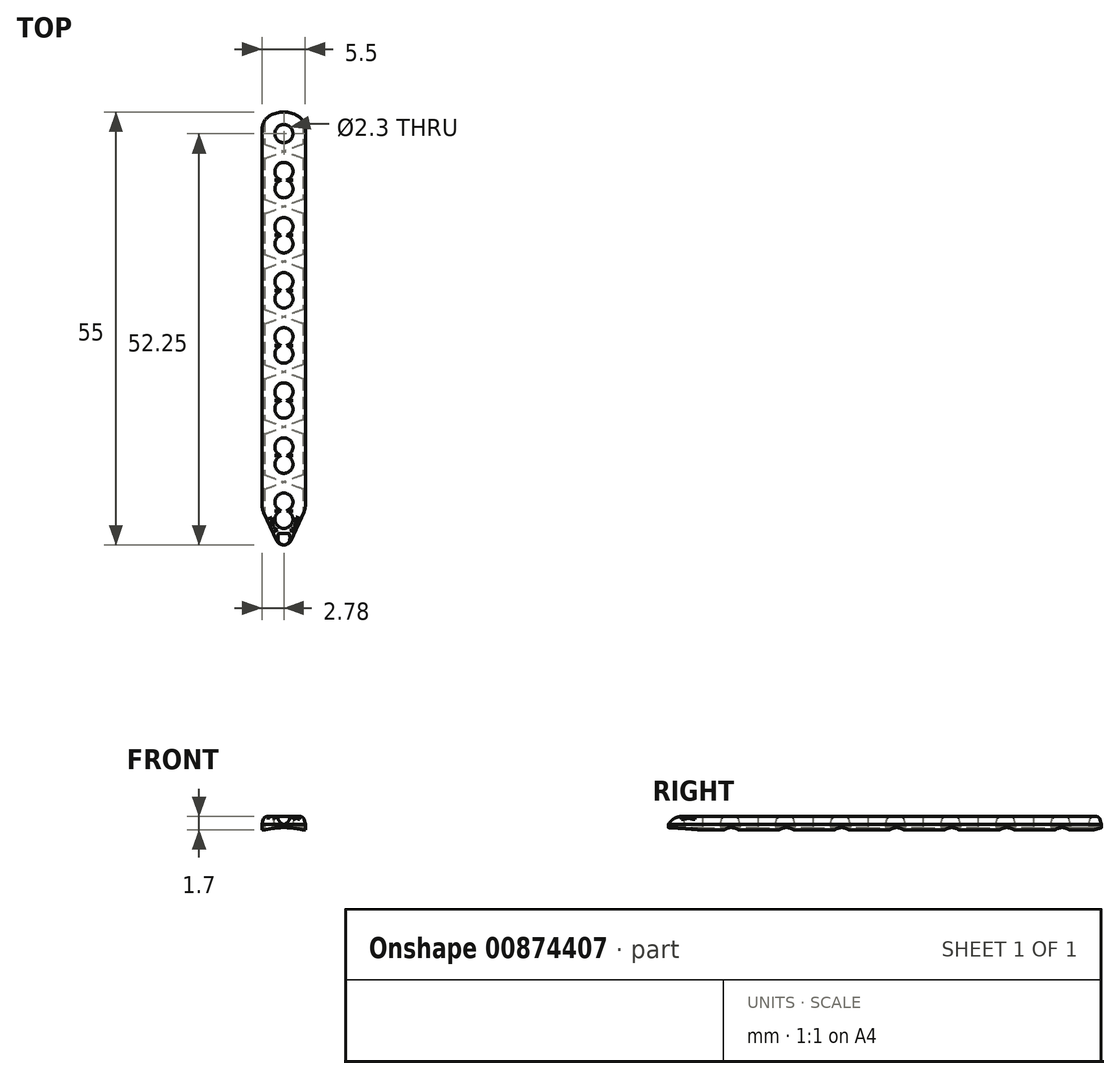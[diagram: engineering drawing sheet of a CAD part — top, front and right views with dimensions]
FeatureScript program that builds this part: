
annotation { "Feature Type Name" : "Feature", "Feature Type Description" : "" }
export const myFeature = defineFeature(function(context is Context, id is Id, definition is map)
    precondition{}
    {
        {
            var Q0;
            Q0=qCreatedBy(makeId("Top.planeOp"),FACE);
            var sketch = newSketch(context, id + "F0", { "sketchPlane" : qUnion([Q0])});
            skLineSegment(sketch, "E0", {"start": v(0, 0) * mm, "end": v(0, -52.25) * mm, "construction": true});
            skLineSegment(sketch, "E1", {"start": v(-2.78, -47.25) * mm, "end": v(-2.78, 0.55) * mm});
            skLineSegment(sketch, "E2", {"start": v(-2.78, 1.42) * mm, "end": v(2.72, 1.42) * mm, "construction": true});
            skLineSegment(sketch, "E3", {"start": v(2.72, 0.57) * mm, "end": v(2.72, -47.25) * mm});
            skArc(sketch, "E4", {"start": v(1.77, 2.26) * mm, "mid": v(0, 2.75) * mm, "end": v(-1.78, 2.28) * mm});
            skLineSegment(sketch, "E5", {"start": v(0, 2.75) * mm, "end": v(0, 0) * mm});
            skPoint(sketch, "E6.visualSharp", {"position": v(-2.78, 1.42) * mm});
            skArc(sketch, "E6.filletArc", {"start": v(-1.78, 2.28) * mm, "mid": v(-2.5, 1.55) * mm, "end": v(-2.78, 0.55) * mm});
            skPoint(sketch, "E7.visualSharp", {"position": v(2.72, 1.42) * mm});
            skArc(sketch, "E7.filletArc", {"start": v(2.72, 0.57) * mm, "mid": v(2.47, 1.54) * mm, "end": v(1.77, 2.26) * mm});
            skPoint(sketch, "E8.visualSharp", {"position": v(0, -52.25) * mm});
            skArc(sketch, "E8.filletArc", {"start": v(-0.91, -51.67) * mm, "mid": v(0, -52.25) * mm, "end": v(0.9, -51.67) * mm});
            skCircle(sketch, "E9", {"center": v(0, 0) * mm, "radius": 1.15 * mm, "construction": true});
            skPoint(sketch, "E10", {"position": v(0, 1.15) * mm});
            skLineSegment(sketch, "E11", {"start": v(-2.78, -47.25) * mm, "end": v(2.72, -47.25) * mm, "construction": true});
            skLineSegment(sketch, "E12", {"start": v(-2.59, -48.1) * mm, "end": v(-0.91, -51.67) * mm});
            skLineSegment(sketch, "E13", {"start": v(0.9, -51.67) * mm, "end": v(2.54, -48.08) * mm});
            skArc(sketch, "E14", {"start": v(-2.78, -47.25) * mm, "mid": v(-2.73, -47.68) * mm, "end": v(-2.59, -48.1) * mm});
            skArc(sketch, "E15", {"start": v(2.54, -48.08) * mm, "mid": v(2.68, -47.68) * mm, "end": v(2.72, -47.25) * mm});
            skSolve(sketch);
        }
        {
            var Q0;
            Q0=makeQuery(id+"F0.imprint","IMPRINT",FACE,{"disambiguationData":[TD([[makeQuery(id+"F0.imprint","IMPRINT",EDGE,{"derivedFrom":sQuery(id+"F0.wireOp",EDGE,"E1")}),-1.0]])]});
            extrude(context, id + "F1", {"entities" : qUnion([Q0]), "depth" : 1.7 * mm, "offsetDistance" : 25 * mm});
        }
        {
            var Q0;
            Q0=qCreatedBy(makeId("Right.planeOp"),FACE);
            var sketch = newSketch(context, id + "F2", { "sketchPlane" : qUnion([Q0])});
            skCircle(sketch, "E16", {"center": v(-44.25, -1.2) * mm, "radius": 1.5 * mm});
            skPoint(sketch, "E17", {"position": v(-44.25, 0.3) * mm});
            skPoint(sketch, "E18", {"position": v(-44.25, 0) * mm});
            skCircle(sketch, "E19.1.0.0", {"center": v(-37.25, -1.2) * mm, "radius": 1.5 * mm});
            skCircle(sketch, "E19.2.0.0", {"center": v(-30.25, -1.2) * mm, "radius": 1.5 * mm});
            skCircle(sketch, "E19.3.0.0", {"center": v(-23.25, -1.2) * mm, "radius": 1.5 * mm});
            skCircle(sketch, "E19.4.0.0", {"center": v(-16.25, -1.2) * mm, "radius": 1.5 * mm});
            skCircle(sketch, "E19.5.0.0", {"center": v(-9.25, -1.2) * mm, "radius": 1.5 * mm});
            skCircle(sketch, "E19.6.0.0", {"center": v(-2.25, -1.2) * mm, "radius": 1.5 * mm});
            skLineSegment(sketch, "E19.direction1", {"start": v(-44.25, -1.2) * mm, "end": v(-37.25, -1.2) * mm, "construction": true});
            skSolve(sketch);
        }
        {
            var Q0;
            Q0 = qSketchRegion(id + "F2", true);
            extrude(context, id + "F3", {"entities" : qUnion([Q0]), "operationType" : NewBodyOperationType.REMOVE, "depth" : 25 * mm, "offsetDistance" : 25 * mm, "hasSecondDirection" : true, "secondDirectionOppositeDirection" : true, "secondDirectionDepth" : 25 * mm});
        }
        {
            var Q0;
            Q0=qCreatedBy(makeId("Top.planeOp"),FACE);
            var sketch = newSketch(context, id + "F4", { "sketchPlane" : qUnion([Q0])});
            skCircle(sketch, "E20", {"center": v(0, 0) * mm, "radius": 1.15 * mm});
            skArc(sketch, "E21", {"start": v(0.34, -5.9) * mm, "mid": v(0, -3.65) * mm, "end": v(-0.34, -5.9) * mm});
            skArc(sketch, "E22", {"start": v(-0.34, -5.9) * mm, "mid": v(0, -8.15) * mm, "end": v(0.34, -5.9) * mm});
            skLineSegment(sketch, "E23", {"start": v(0, -7) * mm, "end": v(0, -4.8) * mm, "construction": true});
            skPoint(sketch, "E24", {"position": v(0, -3.65) * mm});
            skPoint(sketch, "E25", {"position": v(0, -8.15) * mm});
            skPoint(sketch, "E26", {"position": v(0, -1.15) * mm});
            skArc(sketch, "E27.0.1.0", {"start": v(0.34, -12.9) * mm, "mid": v(0, -10.65) * mm, "end": v(-0.34, -12.9) * mm});
            skArc(sketch, "E27.0.1.1", {"start": v(-0.34, -12.9) * mm, "mid": v(0, -15.15) * mm, "end": v(0.34, -12.9) * mm});
            skLineSegment(sketch, "E27.0.1.2", {"start": v(0, -14) * mm, "end": v(0, -11.8) * mm, "construction": true});
            skArc(sketch, "E27.0.2.0", {"start": v(0.34, -19.9) * mm, "mid": v(0, -17.65) * mm, "end": v(-0.34, -19.9) * mm});
            skArc(sketch, "E27.0.2.1", {"start": v(-0.34, -19.9) * mm, "mid": v(0, -22.15) * mm, "end": v(0.34, -19.9) * mm});
            skLineSegment(sketch, "E27.0.2.2", {"start": v(0, -21) * mm, "end": v(0, -18.8) * mm, "construction": true});
            skArc(sketch, "E27.0.3.0", {"start": v(0.34, -26.9) * mm, "mid": v(0, -24.65) * mm, "end": v(-0.34, -26.9) * mm});
            skArc(sketch, "E27.0.3.1", {"start": v(-0.34, -26.9) * mm, "mid": v(0, -29.15) * mm, "end": v(0.34, -26.9) * mm});
            skLineSegment(sketch, "E27.0.3.2", {"start": v(0, -28) * mm, "end": v(0, -25.8) * mm, "construction": true});
            skArc(sketch, "E27.0.4.0", {"start": v(0.34, -33.9) * mm, "mid": v(0, -31.65) * mm, "end": v(-0.34, -33.9) * mm});
            skArc(sketch, "E27.0.4.1", {"start": v(-0.34, -33.9) * mm, "mid": v(0, -36.15) * mm, "end": v(0.34, -33.9) * mm});
            skLineSegment(sketch, "E27.0.4.2", {"start": v(0, -35) * mm, "end": v(0, -32.8) * mm, "construction": true});
            skArc(sketch, "E27.0.5.0", {"start": v(0.34, -40.9) * mm, "mid": v(0, -38.65) * mm, "end": v(-0.34, -40.9) * mm});
            skArc(sketch, "E27.0.5.1", {"start": v(-0.34, -40.9) * mm, "mid": v(0, -43.15) * mm, "end": v(0.34, -40.9) * mm});
            skLineSegment(sketch, "E27.0.5.2", {"start": v(0, -42) * mm, "end": v(0, -39.8) * mm, "construction": true});
            skArc(sketch, "E27.0.6.0", {"start": v(0.34, -47.9) * mm, "mid": v(0, -45.65) * mm, "end": v(-0.34, -47.9) * mm});
            skArc(sketch, "E27.0.6.1", {"start": v(-0.34, -47.9) * mm, "mid": v(0, -50.15) * mm, "end": v(0.34, -47.9) * mm});
            skLineSegment(sketch, "E27.0.6.2", {"start": v(0, -49) * mm, "end": v(0, -46.8) * mm, "construction": true});
            skLineSegment(sketch, "E27.direction1", {"start": v(-0.34, -5.9) * mm, "end": v(11.96, -5.9) * mm, "construction": true});
            skLineSegment(sketch, "E27.direction2", {"start": v(-0.34, -5.9) * mm, "end": v(-0.34, -12.9) * mm, "construction": true});
            skSolve(sketch);
        }
        {
            var Q0;
            Q0=qCreatedBy(makeId("Right.planeOp"),FACE);
            var sketch = newSketch(context, id + "F5", { "sketchPlane" : qUnion([Q0])});
            skLineSegment(sketch, "E28", {"start": v(-52.25, 0.7) * mm, "end": v(-52.25, 1.7) * mm});
            skLineSegment(sketch, "E29", {"start": v(-52.25, 1.7) * mm, "end": v(-50.25, 1.7) * mm});
            skArc(sketch, "E30", {"start": v(-50.25, 1.7) * mm, "mid": v(-51.4, 1.5) * mm, "end": v(-52.25, 0.7) * mm});
            skSolve(sketch);
        }
        {
            var Q0;
            Q0 = qSketchRegion(id + "F4", true);
            extrude(context, id + "F6", {"entities" : qUnion([Q0]), "operationType" : NewBodyOperationType.REMOVE, "endBound" : BoundingType.THROUGH_ALL, "depth" : 25 * mm, "offsetDistance" : 25 * mm});
        }
        {
            var Q0;
            Q0=makeQuery(id+"F1.opExtrude","CAP_FACE",FACE,{"disambiguationData":[OSD([sQuery(id+"F0.wireOp",EDGE,"E1"),sQuery(id+"F0.wireOp",EDGE,"E3"),sQuery(id+"F0.wireOp",EDGE,"E4"),sQuery(id+"F0.wireOp",EDGE,"E6.filletArc"),sQuery(id+"F0.wireOp",EDGE,"E7.filletArc"),sQuery(id+"F0.wireOp",EDGE,"E8.filletArc"),sQuery(id+"F0.wireOp",EDGE,"E12"),sQuery(id+"F0.wireOp",EDGE,"E13"),sQuery(id+"F0.wireOp",EDGE,"E14"),sQuery(id+"F0.wireOp",EDGE,"E15")])],"isStart":false});
            chamfer(context, id + "F7", {"entities" : qUnion([Q0]), "chamferType" : ChamferType.TWO_OFFSETS, "width1" : 1 * mm, "oppositeDirection" : false, "width2" : 0.25 * mm, "tangentPropagation" : true});
        }
        {
            var Q0;
            {var subQ0=makeQuery(id+"F1.opExtrude","CAP_FACE",FACE,{"disambiguationData":[OSD([sQuery(id+"F0.wireOp",EDGE,"E1"),sQuery(id+"F0.wireOp",EDGE,"E3"),sQuery(id+"F0.wireOp",EDGE,"E4"),sQuery(id+"F0.wireOp",EDGE,"E6.filletArc"),sQuery(id+"F0.wireOp",EDGE,"E7.filletArc"),sQuery(id+"F0.wireOp",EDGE,"E8.filletArc"),sQuery(id+"F0.wireOp",EDGE,"E12"),sQuery(id+"F0.wireOp",EDGE,"E13"),sQuery(id+"F0.wireOp",EDGE,"E14"),sQuery(id+"F0.wireOp",EDGE,"E15")])],"isStart":false});Q0=makeQuery(id+"F7.opChamfer","BLEND_EDGE",EDGE,{"blendedFrom":[makeQuery(id+"F6.boolean.opBoolean","INTERSECT",EDGE,{"derivedFrom":[subQ0,makeQuery(id+"F6.opExtrude","SWEPT_FACE",FACE,{"disambiguationData":[OSD([sQuery(id+"F4.wireOp",EDGE,"E27.0.6.1")])]})]}),subQ0],"blendedInto":[subQ0]});}
            var Q1;
            {var subQ0=makeQuery(id+"F1.opExtrude","CAP_FACE",FACE,{"disambiguationData":[OSD([sQuery(id+"F0.wireOp",EDGE,"E1"),sQuery(id+"F0.wireOp",EDGE,"E3"),sQuery(id+"F0.wireOp",EDGE,"E4"),sQuery(id+"F0.wireOp",EDGE,"E6.filletArc"),sQuery(id+"F0.wireOp",EDGE,"E7.filletArc"),sQuery(id+"F0.wireOp",EDGE,"E8.filletArc"),sQuery(id+"F0.wireOp",EDGE,"E12"),sQuery(id+"F0.wireOp",EDGE,"E13"),sQuery(id+"F0.wireOp",EDGE,"E14"),sQuery(id+"F0.wireOp",EDGE,"E15")])],"isStart":false});Q1=makeQuery(id+"F7.opChamfer","BLEND_EDGE",EDGE,{"blendedFrom":[makeQuery(id+"F6.boolean.opBoolean","INTERSECT",EDGE,{"derivedFrom":[subQ0,makeQuery(id+"F6.opExtrude","SWEPT_FACE",FACE,{"disambiguationData":[OSD([sQuery(id+"F4.wireOp",EDGE,"E27.0.6.0")])]})]}),subQ0],"blendedInto":[subQ0]});}
            var Q2;
            {var subQ0=makeQuery(id+"F1.opExtrude","CAP_FACE",FACE,{"disambiguationData":[OSD([sQuery(id+"F0.wireOp",EDGE,"E1"),sQuery(id+"F0.wireOp",EDGE,"E3"),sQuery(id+"F0.wireOp",EDGE,"E4"),sQuery(id+"F0.wireOp",EDGE,"E6.filletArc"),sQuery(id+"F0.wireOp",EDGE,"E7.filletArc"),sQuery(id+"F0.wireOp",EDGE,"E8.filletArc"),sQuery(id+"F0.wireOp",EDGE,"E12"),sQuery(id+"F0.wireOp",EDGE,"E13"),sQuery(id+"F0.wireOp",EDGE,"E14"),sQuery(id+"F0.wireOp",EDGE,"E15")])],"isStart":false});Q2=makeQuery(id+"F7.opChamfer","BLEND_EDGE",EDGE,{"blendedFrom":[makeQuery(id+"F6.boolean.opBoolean","INTERSECT",EDGE,{"derivedFrom":[subQ0,makeQuery(id+"F6.opExtrude","SWEPT_FACE",FACE,{"disambiguationData":[OSD([sQuery(id+"F4.wireOp",EDGE,"E27.0.5.1")])]})]}),subQ0],"blendedInto":[subQ0]});}
            var Q3;
            {var subQ0=makeQuery(id+"F1.opExtrude","CAP_FACE",FACE,{"disambiguationData":[OSD([sQuery(id+"F0.wireOp",EDGE,"E1"),sQuery(id+"F0.wireOp",EDGE,"E3"),sQuery(id+"F0.wireOp",EDGE,"E4"),sQuery(id+"F0.wireOp",EDGE,"E6.filletArc"),sQuery(id+"F0.wireOp",EDGE,"E7.filletArc"),sQuery(id+"F0.wireOp",EDGE,"E8.filletArc"),sQuery(id+"F0.wireOp",EDGE,"E12"),sQuery(id+"F0.wireOp",EDGE,"E13"),sQuery(id+"F0.wireOp",EDGE,"E14"),sQuery(id+"F0.wireOp",EDGE,"E15")])],"isStart":false});Q3=makeQuery(id+"F7.opChamfer","BLEND_EDGE",EDGE,{"blendedFrom":[makeQuery(id+"F6.boolean.opBoolean","INTERSECT",EDGE,{"derivedFrom":[subQ0,makeQuery(id+"F6.opExtrude","SWEPT_FACE",FACE,{"disambiguationData":[OSD([sQuery(id+"F4.wireOp",EDGE,"E27.0.5.0")])]})]}),subQ0],"blendedInto":[subQ0]});}
            var Q4;
            {var subQ0=makeQuery(id+"F1.opExtrude","CAP_FACE",FACE,{"disambiguationData":[OSD([sQuery(id+"F0.wireOp",EDGE,"E1"),sQuery(id+"F0.wireOp",EDGE,"E3"),sQuery(id+"F0.wireOp",EDGE,"E4"),sQuery(id+"F0.wireOp",EDGE,"E6.filletArc"),sQuery(id+"F0.wireOp",EDGE,"E7.filletArc"),sQuery(id+"F0.wireOp",EDGE,"E8.filletArc"),sQuery(id+"F0.wireOp",EDGE,"E12"),sQuery(id+"F0.wireOp",EDGE,"E13"),sQuery(id+"F0.wireOp",EDGE,"E14"),sQuery(id+"F0.wireOp",EDGE,"E15")])],"isStart":false});Q4=makeQuery(id+"F7.opChamfer","BLEND_EDGE",EDGE,{"blendedFrom":[makeQuery(id+"F6.boolean.opBoolean","INTERSECT",EDGE,{"derivedFrom":[subQ0,makeQuery(id+"F6.opExtrude","SWEPT_FACE",FACE,{"disambiguationData":[OSD([sQuery(id+"F4.wireOp",EDGE,"E27.0.4.1")])]})]}),subQ0],"blendedInto":[subQ0]});}
            var Q5;
            {var subQ0=makeQuery(id+"F1.opExtrude","CAP_FACE",FACE,{"disambiguationData":[OSD([sQuery(id+"F0.wireOp",EDGE,"E1"),sQuery(id+"F0.wireOp",EDGE,"E3"),sQuery(id+"F0.wireOp",EDGE,"E4"),sQuery(id+"F0.wireOp",EDGE,"E6.filletArc"),sQuery(id+"F0.wireOp",EDGE,"E7.filletArc"),sQuery(id+"F0.wireOp",EDGE,"E8.filletArc"),sQuery(id+"F0.wireOp",EDGE,"E12"),sQuery(id+"F0.wireOp",EDGE,"E13"),sQuery(id+"F0.wireOp",EDGE,"E14"),sQuery(id+"F0.wireOp",EDGE,"E15")])],"isStart":false});Q5=makeQuery(id+"F7.opChamfer","BLEND_EDGE",EDGE,{"blendedFrom":[makeQuery(id+"F6.boolean.opBoolean","INTERSECT",EDGE,{"derivedFrom":[subQ0,makeQuery(id+"F6.opExtrude","SWEPT_FACE",FACE,{"disambiguationData":[OSD([sQuery(id+"F4.wireOp",EDGE,"E27.0.4.0")])]})]}),subQ0],"blendedInto":[subQ0]});}
            var Q6;
            {var subQ0=makeQuery(id+"F1.opExtrude","CAP_FACE",FACE,{"disambiguationData":[OSD([sQuery(id+"F0.wireOp",EDGE,"E1"),sQuery(id+"F0.wireOp",EDGE,"E3"),sQuery(id+"F0.wireOp",EDGE,"E4"),sQuery(id+"F0.wireOp",EDGE,"E6.filletArc"),sQuery(id+"F0.wireOp",EDGE,"E7.filletArc"),sQuery(id+"F0.wireOp",EDGE,"E8.filletArc"),sQuery(id+"F0.wireOp",EDGE,"E12"),sQuery(id+"F0.wireOp",EDGE,"E13"),sQuery(id+"F0.wireOp",EDGE,"E14"),sQuery(id+"F0.wireOp",EDGE,"E15")])],"isStart":false});Q6=makeQuery(id+"F7.opChamfer","BLEND_EDGE",EDGE,{"blendedFrom":[makeQuery(id+"F6.boolean.opBoolean","INTERSECT",EDGE,{"derivedFrom":[subQ0,makeQuery(id+"F6.opExtrude","SWEPT_FACE",FACE,{"disambiguationData":[OSD([sQuery(id+"F4.wireOp",EDGE,"E27.0.3.1")])]})]}),subQ0],"blendedInto":[subQ0]});}
            var Q7;
            {var subQ0=makeQuery(id+"F1.opExtrude","CAP_FACE",FACE,{"disambiguationData":[OSD([sQuery(id+"F0.wireOp",EDGE,"E1"),sQuery(id+"F0.wireOp",EDGE,"E3"),sQuery(id+"F0.wireOp",EDGE,"E4"),sQuery(id+"F0.wireOp",EDGE,"E6.filletArc"),sQuery(id+"F0.wireOp",EDGE,"E7.filletArc"),sQuery(id+"F0.wireOp",EDGE,"E8.filletArc"),sQuery(id+"F0.wireOp",EDGE,"E12"),sQuery(id+"F0.wireOp",EDGE,"E13"),sQuery(id+"F0.wireOp",EDGE,"E14"),sQuery(id+"F0.wireOp",EDGE,"E15")])],"isStart":false});Q7=makeQuery(id+"F7.opChamfer","BLEND_EDGE",EDGE,{"blendedFrom":[makeQuery(id+"F6.boolean.opBoolean","INTERSECT",EDGE,{"derivedFrom":[subQ0,makeQuery(id+"F6.opExtrude","SWEPT_FACE",FACE,{"disambiguationData":[OSD([sQuery(id+"F4.wireOp",EDGE,"E27.0.3.0")])]})]}),subQ0],"blendedInto":[subQ0]});}
            var Q8;
            {var subQ0=makeQuery(id+"F1.opExtrude","CAP_FACE",FACE,{"disambiguationData":[OSD([sQuery(id+"F0.wireOp",EDGE,"E1"),sQuery(id+"F0.wireOp",EDGE,"E3"),sQuery(id+"F0.wireOp",EDGE,"E4"),sQuery(id+"F0.wireOp",EDGE,"E6.filletArc"),sQuery(id+"F0.wireOp",EDGE,"E7.filletArc"),sQuery(id+"F0.wireOp",EDGE,"E8.filletArc"),sQuery(id+"F0.wireOp",EDGE,"E12"),sQuery(id+"F0.wireOp",EDGE,"E13"),sQuery(id+"F0.wireOp",EDGE,"E14"),sQuery(id+"F0.wireOp",EDGE,"E15")])],"isStart":false});Q8=makeQuery(id+"F7.opChamfer","BLEND_EDGE",EDGE,{"blendedFrom":[makeQuery(id+"F6.boolean.opBoolean","INTERSECT",EDGE,{"derivedFrom":[subQ0,makeQuery(id+"F6.opExtrude","SWEPT_FACE",FACE,{"disambiguationData":[OSD([sQuery(id+"F4.wireOp",EDGE,"E27.0.2.0")])]})]}),subQ0],"blendedInto":[subQ0]});}
            var Q9;
            {var subQ0=makeQuery(id+"F1.opExtrude","CAP_FACE",FACE,{"disambiguationData":[OSD([sQuery(id+"F0.wireOp",EDGE,"E1"),sQuery(id+"F0.wireOp",EDGE,"E3"),sQuery(id+"F0.wireOp",EDGE,"E4"),sQuery(id+"F0.wireOp",EDGE,"E6.filletArc"),sQuery(id+"F0.wireOp",EDGE,"E7.filletArc"),sQuery(id+"F0.wireOp",EDGE,"E8.filletArc"),sQuery(id+"F0.wireOp",EDGE,"E12"),sQuery(id+"F0.wireOp",EDGE,"E13"),sQuery(id+"F0.wireOp",EDGE,"E14"),sQuery(id+"F0.wireOp",EDGE,"E15")])],"isStart":false});Q9=makeQuery(id+"F7.opChamfer","BLEND_EDGE",EDGE,{"blendedFrom":[makeQuery(id+"F6.boolean.opBoolean","INTERSECT",EDGE,{"derivedFrom":[subQ0,makeQuery(id+"F6.opExtrude","SWEPT_FACE",FACE,{"disambiguationData":[OSD([sQuery(id+"F4.wireOp",EDGE,"E27.0.2.1")])]})]}),subQ0],"blendedInto":[subQ0]});}
            var Q10;
            {var subQ0=makeQuery(id+"F1.opExtrude","CAP_FACE",FACE,{"disambiguationData":[OSD([sQuery(id+"F0.wireOp",EDGE,"E1"),sQuery(id+"F0.wireOp",EDGE,"E3"),sQuery(id+"F0.wireOp",EDGE,"E4"),sQuery(id+"F0.wireOp",EDGE,"E6.filletArc"),sQuery(id+"F0.wireOp",EDGE,"E7.filletArc"),sQuery(id+"F0.wireOp",EDGE,"E8.filletArc"),sQuery(id+"F0.wireOp",EDGE,"E12"),sQuery(id+"F0.wireOp",EDGE,"E13"),sQuery(id+"F0.wireOp",EDGE,"E14"),sQuery(id+"F0.wireOp",EDGE,"E15")])],"isStart":false});Q10=makeQuery(id+"F7.opChamfer","BLEND_EDGE",EDGE,{"blendedFrom":[makeQuery(id+"F6.boolean.opBoolean","INTERSECT",EDGE,{"derivedFrom":[subQ0,makeQuery(id+"F6.opExtrude","SWEPT_FACE",FACE,{"disambiguationData":[OSD([sQuery(id+"F4.wireOp",EDGE,"E27.0.1.1")])]})]}),subQ0],"blendedInto":[subQ0]});}
            var Q11;
            {var subQ0=makeQuery(id+"F1.opExtrude","CAP_FACE",FACE,{"disambiguationData":[OSD([sQuery(id+"F0.wireOp",EDGE,"E1"),sQuery(id+"F0.wireOp",EDGE,"E3"),sQuery(id+"F0.wireOp",EDGE,"E4"),sQuery(id+"F0.wireOp",EDGE,"E6.filletArc"),sQuery(id+"F0.wireOp",EDGE,"E7.filletArc"),sQuery(id+"F0.wireOp",EDGE,"E8.filletArc"),sQuery(id+"F0.wireOp",EDGE,"E12"),sQuery(id+"F0.wireOp",EDGE,"E13"),sQuery(id+"F0.wireOp",EDGE,"E14"),sQuery(id+"F0.wireOp",EDGE,"E15")])],"isStart":false});Q11=makeQuery(id+"F7.opChamfer","BLEND_EDGE",EDGE,{"blendedFrom":[makeQuery(id+"F6.boolean.opBoolean","INTERSECT",EDGE,{"derivedFrom":[subQ0,makeQuery(id+"F6.opExtrude","SWEPT_FACE",FACE,{"disambiguationData":[OSD([sQuery(id+"F4.wireOp",EDGE,"E27.0.1.0")])]})]}),subQ0],"blendedInto":[subQ0]});}
            var Q12;
            {var subQ0=makeQuery(id+"F1.opExtrude","CAP_FACE",FACE,{"disambiguationData":[OSD([sQuery(id+"F0.wireOp",EDGE,"E1"),sQuery(id+"F0.wireOp",EDGE,"E3"),sQuery(id+"F0.wireOp",EDGE,"E4"),sQuery(id+"F0.wireOp",EDGE,"E6.filletArc"),sQuery(id+"F0.wireOp",EDGE,"E7.filletArc"),sQuery(id+"F0.wireOp",EDGE,"E8.filletArc"),sQuery(id+"F0.wireOp",EDGE,"E12"),sQuery(id+"F0.wireOp",EDGE,"E13"),sQuery(id+"F0.wireOp",EDGE,"E14"),sQuery(id+"F0.wireOp",EDGE,"E15")])],"isStart":false});Q12=makeQuery(id+"F7.opChamfer","BLEND_EDGE",EDGE,{"blendedFrom":[makeQuery(id+"F6.boolean.opBoolean","INTERSECT",EDGE,{"derivedFrom":[subQ0,makeQuery(id+"F6.opExtrude","SWEPT_FACE",FACE,{"disambiguationData":[OSD([sQuery(id+"F4.wireOp",EDGE,"E22")])]})]}),subQ0],"blendedInto":[subQ0]});}
            var Q13;
            {var subQ0=makeQuery(id+"F1.opExtrude","CAP_FACE",FACE,{"disambiguationData":[OSD([sQuery(id+"F0.wireOp",EDGE,"E1"),sQuery(id+"F0.wireOp",EDGE,"E3"),sQuery(id+"F0.wireOp",EDGE,"E4"),sQuery(id+"F0.wireOp",EDGE,"E6.filletArc"),sQuery(id+"F0.wireOp",EDGE,"E7.filletArc"),sQuery(id+"F0.wireOp",EDGE,"E8.filletArc"),sQuery(id+"F0.wireOp",EDGE,"E12"),sQuery(id+"F0.wireOp",EDGE,"E13"),sQuery(id+"F0.wireOp",EDGE,"E14"),sQuery(id+"F0.wireOp",EDGE,"E15")])],"isStart":false});Q13=makeQuery(id+"F7.opChamfer","BLEND_EDGE",EDGE,{"blendedFrom":[makeQuery(id+"F6.boolean.opBoolean","INTERSECT",EDGE,{"derivedFrom":[subQ0,makeQuery(id+"F6.opExtrude","SWEPT_FACE",FACE,{"disambiguationData":[OSD([sQuery(id+"F4.wireOp",EDGE,"E21")])]})]}),subQ0],"blendedInto":[subQ0]});}
            var Q14;
            {var subQ0=makeQuery(id+"F1.opExtrude","CAP_FACE",FACE,{"disambiguationData":[OSD([sQuery(id+"F0.wireOp",EDGE,"E1"),sQuery(id+"F0.wireOp",EDGE,"E3"),sQuery(id+"F0.wireOp",EDGE,"E4"),sQuery(id+"F0.wireOp",EDGE,"E6.filletArc"),sQuery(id+"F0.wireOp",EDGE,"E7.filletArc"),sQuery(id+"F0.wireOp",EDGE,"E8.filletArc"),sQuery(id+"F0.wireOp",EDGE,"E12"),sQuery(id+"F0.wireOp",EDGE,"E13"),sQuery(id+"F0.wireOp",EDGE,"E14"),sQuery(id+"F0.wireOp",EDGE,"E15")])],"isStart":false});Q14=makeQuery(id+"F7.opChamfer","BLEND_EDGE",EDGE,{"blendedFrom":[makeQuery(id+"F6.boolean.opBoolean","INTERSECT",EDGE,{"derivedFrom":[subQ0,makeQuery(id+"F6.opExtrude","SWEPT_FACE",FACE,{"disambiguationData":[OSD([sQuery(id+"F4.wireOp",EDGE,"E20")])]})]}),subQ0],"blendedInto":[subQ0]});}
            fillet(context, id + "F8", {"entities" : qUnion([Q0, Q1, Q2, Q3, Q4, Q5, Q6, Q7, Q8, Q9, Q10, Q11, Q12, Q13, Q14]), "radius" : 0.25 * mm, "tangentPropagation" : true, "allowEdgeOverflow" : false});
        }
        {
            var Q0;
            {var subQ0=sQuery(id+"F0.wireOp",EDGE,"E12");Q0=makeQuery(id+"F7.opChamfer","BLEND_EDGE",EDGE,{"blendedFrom":[makeQuery(id+"F1.opExtrude","CAP_EDGE",EDGE,{"disambiguationData":[OSD([subQ0])],"isStart":false}),makeQuery(id+"F1.opExtrude","CAP_FACE",FACE,{"disambiguationData":[OSD([sQuery(id+"F0.wireOp",EDGE,"E1"),sQuery(id+"F0.wireOp",EDGE,"E3"),sQuery(id+"F0.wireOp",EDGE,"E4"),sQuery(id+"F0.wireOp",EDGE,"E6.filletArc"),sQuery(id+"F0.wireOp",EDGE,"E7.filletArc"),sQuery(id+"F0.wireOp",EDGE,"E8.filletArc"),subQ0,sQuery(id+"F0.wireOp",EDGE,"E13"),sQuery(id+"F0.wireOp",EDGE,"E14"),sQuery(id+"F0.wireOp",EDGE,"E15")])],"isStart":false})],"blendedInto":[makeQuery(id+"F1.opExtrude","CAP_FACE",FACE,{"disambiguationData":[OSD([sQuery(id+"F0.wireOp",EDGE,"E1"),sQuery(id+"F0.wireOp",EDGE,"E3"),sQuery(id+"F0.wireOp",EDGE,"E4"),sQuery(id+"F0.wireOp",EDGE,"E6.filletArc"),sQuery(id+"F0.wireOp",EDGE,"E7.filletArc"),sQuery(id+"F0.wireOp",EDGE,"E8.filletArc"),subQ0,sQuery(id+"F0.wireOp",EDGE,"E13"),sQuery(id+"F0.wireOp",EDGE,"E14"),sQuery(id+"F0.wireOp",EDGE,"E15")])],"isStart":false})]});}
            fillet(context, id + "F9", {"entities" : qUnion([Q0]), "radius" : 0.5 * mm, "tangentPropagation" : true, "allowEdgeOverflow" : false});
        }
        {
            var Q0;
            Q0=makeQuery(id+"F1.opExtrude","CAP_EDGE",EDGE,{"disambiguationData":[OSD([sQuery(id+"F0.wireOp",EDGE,"E12")])],"isStart":true});
            fillet(context, id + "F10", {"entities" : qUnion([Q0]), "radius" : 0.2 * mm, "tangentPropagation" : true, "allowEdgeOverflow" : false});
        }
        {
            var Q0;
            Q0=qCreatedBy(makeId("Front.planeOp"),FACE);
            var sketch = newSketch(context, id + "F11", { "sketchPlane" : qUnion([Q0])});
            skCircle(sketch, "E31", {"center": v(0, -9.7) * mm, "radius": 10 * mm});
            skLineSegment(sketch, "E32", {"start": v(0, 0) * mm, "end": v(0, 0.3) * mm, "construction": true});
            skSolve(sketch);
        }
        {
            var Q0;
            Q0=makeQuery(id+"F11.imprint","IMPRINT",FACE,{"disambiguationData":[TD([[makeQuery(id+"F11.imprint","IMPRINT",EDGE,{"derivedFrom":sQuery(id+"F11.wireOp",EDGE,"E31")}),1.0]])]});
            var Q1;
            Q1=sQuery(id+"F11.wireOp",EDGE,"E31");
            extrude(context, id + "F12", {"entities" : qUnion([Q0]), "operationType" : NewBodyOperationType.REMOVE, "surfaceEntities" : qUnion([Q1]), "endBound" : BoundingType.THROUGH_ALL, "oppositeDirection" : true, "depth" : 25 * mm, "offsetDistance" : 25 * mm, "hasSecondDirection" : true, "secondDirectionBound" : SecondDirectionBoundingType.THROUGH_ALL, "secondDirectionOppositeDirection" : false, "secondDirectionDepth" : 25 * mm});
        }
        {
            var Q0;
            Q0 = qSketchRegion(id + "F5", true);
            extrude(context, id + "F13", {"entities" : qUnion([Q0]), "operationType" : NewBodyOperationType.REMOVE, "endBound" : BoundingType.THROUGH_ALL, "oppositeDirection" : true, "depth" : 25 * mm, "offsetDistance" : 25 * mm, "hasSecondDirection" : true, "secondDirectionBound" : SecondDirectionBoundingType.THROUGH_ALL, "secondDirectionOppositeDirection" : false, "secondDirectionDepth" : 25 * mm});
        }
    });
